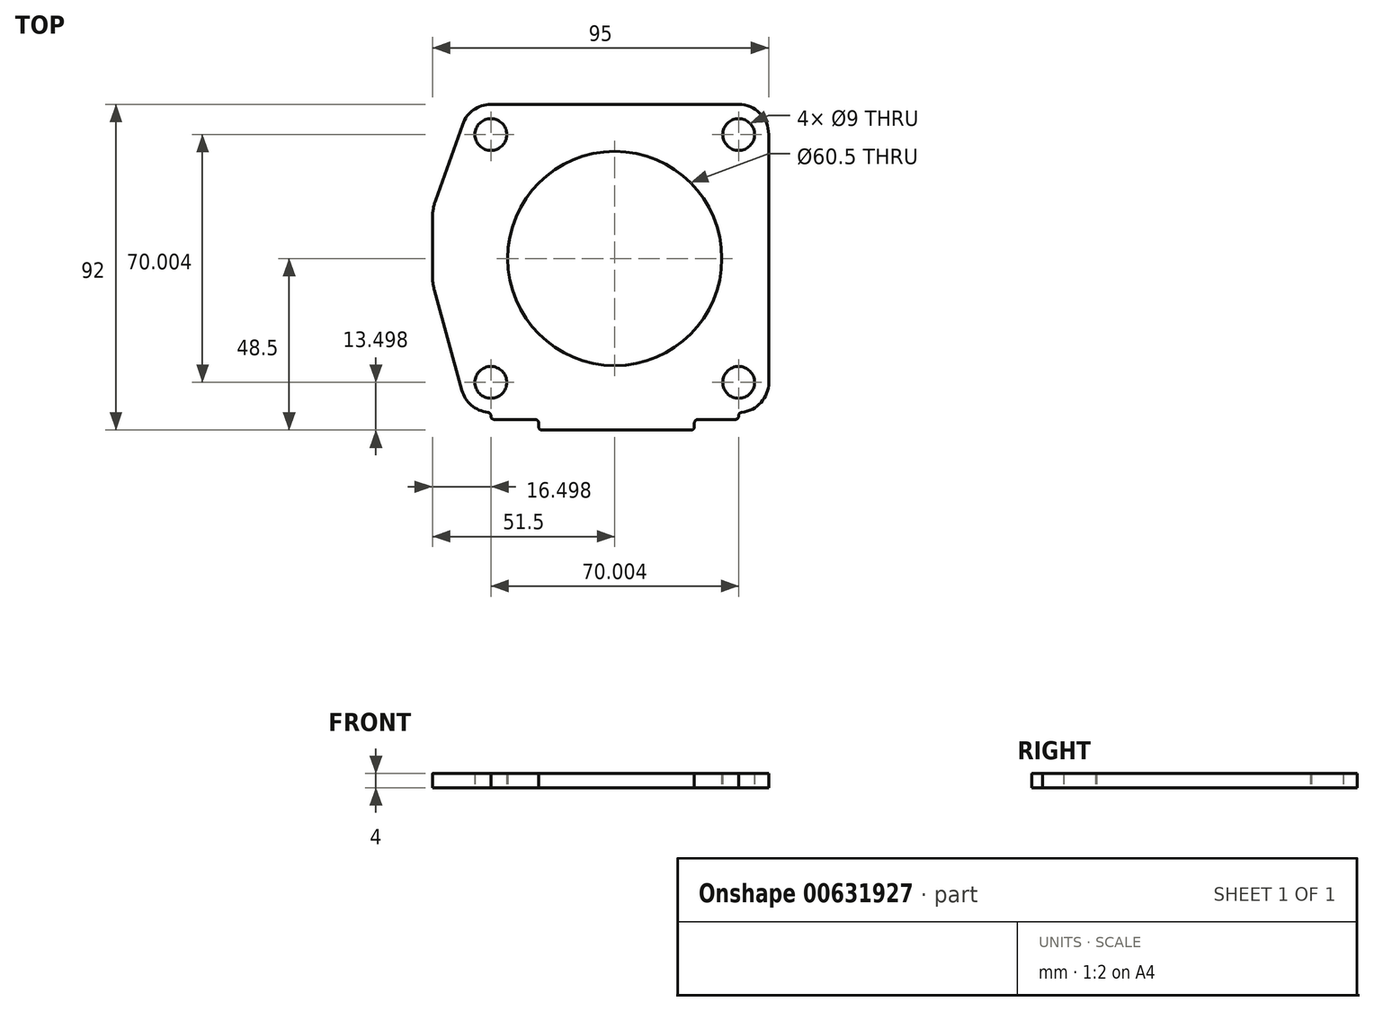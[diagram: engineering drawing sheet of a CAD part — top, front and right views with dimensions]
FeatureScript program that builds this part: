
annotation { "Feature Type Name" : "Feature", "Feature Type Description" : "" }
export const myFeature = defineFeature(function(context is Context, id is Id, definition is map)
    precondition{}
    {
        {
            var Q0;
            Q0=qCreatedBy(makeId("Top.planeOp"),FACE);
            var sketch = newSketch(context, id + "F0", { "sketchPlane" : qUnion([Q0])});
            skCircle(sketch, "E0", {"center": v(0, 0) * mm, "radius": 49.5 * mm, "construction": true});
            skCircle(sketch, "E1", {"center": v(-35, 35) * mm, "radius": 4.5 * mm});
            skLineSegment(sketch, "E2", {"start": v(-35, 35) * mm, "end": v(0, 0) * mm, "construction": true});
            skLineSegment(sketch, "E3", {"start": v(0, 49.5) * mm, "end": v(0, 0) * mm, "construction": true});
            skCircle(sketch, "E4.1.0", {"center": v(-35, -35) * mm, "radius": 4.5 * mm});
            skCircle(sketch, "E4.2.0", {"center": v(35, -35) * mm, "radius": 4.5 * mm});
            skCircle(sketch, "E4.3.0", {"center": v(35, 35) * mm, "radius": 4.5 * mm});
            skCircle(sketch, "E5", {"center": v(-35, 35) * mm, "radius": 8.5 * mm});
            skCircle(sketch, "E6", {"center": v(35, 35) * mm, "radius": 8.5 * mm});
            skCircle(sketch, "E7", {"center": v(35, -35) * mm, "radius": 8.5 * mm});
            skCircle(sketch, "E8", {"center": v(-35, -35) * mm, "radius": 8.5 * mm});
            skLineSegment(sketch, "E9", {"start": v(-35, 43.5) * mm, "end": v(35, 43.5) * mm});
            skLineSegment(sketch, "E10", {"start": v(43.5, 35) * mm, "end": v(43.5, -35) * mm});
            skLineSegment(sketch, "E11", {"start": v(35, -43.5) * mm, "end": v(-35, -43.5) * mm});
            skLineSegment(sketch, "E12", {"start": v(-43.5, -35) * mm, "end": v(-43.5, 35) * mm});
            skCircle(sketch, "E13", {"center": v(0, 0) * mm, "radius": 30.25 * mm});
            skLineSegment(sketch, "E14.bottom", {"start": v(-35, -43.5) * mm, "end": v(35, -43.5) * mm});
            skLineSegment(sketch, "E14.top", {"start": v(-35, -45.5) * mm, "end": v(35, -45.5) * mm});
            skLineSegment(sketch, "E14.left", {"start": v(-35, -43.5) * mm, "end": v(-35, -45.5) * mm});
            skLineSegment(sketch, "E14.right", {"start": v(35, -43.5) * mm, "end": v(35, -45.5) * mm});
            skLineSegment(sketch, "E15.bottom", {"start": v(-21.5, -45.5) * mm, "end": v(22.5, -45.5) * mm});
            skLineSegment(sketch, "E15.top", {"start": v(-21.5, -48.5) * mm, "end": v(22.5, -48.5) * mm});
            skLineSegment(sketch, "E15.left", {"start": v(-21.5, -45.5) * mm, "end": v(-21.5, -48.5) * mm});
            skLineSegment(sketch, "E15.right", {"start": v(22.5, -45.5) * mm, "end": v(22.5, -48.5) * mm});
            skLineSegment(sketch, "E16", {"start": v(-51.5, 14) * mm, "end": v(-51.5, -7) * mm});
            skLineSegment(sketch, "E17", {"start": v(-51.5, 14) * mm, "end": v(-43, 37.85) * mm});
            skLineSegment(sketch, "E18", {"start": v(-51.5, -7) * mm, "end": v(-43.2, -37.25) * mm});
            skSolve(sketch);
        }
        {
            var Q0;
            Q0 = qSketchRegion(id + "F0", true);
            extrude(context, id + "F1", {"entities" : qUnion([Q0]), "depth" : 4 * mm, "offsetDistance" : 25 * mm});
        }
        {
            var Q0;
            Q0=makeQuery(id+"F1.opExtrude","SWEPT_EDGE",EDGE,{"disambiguationData":[OSD([sQuery(id+"F0.wireOp",EDGE,"E16"),sQuery(id+"F0.wireOp",EDGE,"E17")])]});
            var Q1;
            Q1=makeQuery(id+"F1.opExtrude","SWEPT_EDGE",EDGE,{"disambiguationData":[OSD([sQuery(id+"F0.wireOp",EDGE,"E16"),sQuery(id+"F0.wireOp",EDGE,"E18")])]});
            fillet(context, id + "F2", {"entities" : qUnion([Q0, Q1]), "radius" : 15 * mm, "tangentPropagation" : true, "allowEdgeOverflow" : false});
        }
        {
            var Q0;
            Q0=makeQuery(id+"F1.opExtrude","SWEPT_EDGE",EDGE,{"disambiguationData":[OSD([sQuery(id+"F0.wireOp",EDGE,"E8"),sQuery(id+"F0.wireOp",EDGE,"E14.bottom"),sQuery(id+"F0.wireOp",EDGE,"E14.left")])]});
            var Q1;
            Q1=makeQuery(id+"F1.opExtrude","SWEPT_EDGE",EDGE,{"disambiguationData":[OSD([sQuery(id+"F0.wireOp",EDGE,"E14.top"),sQuery(id+"F0.wireOp",EDGE,"E15.bottom"),sQuery(id+"F0.wireOp",EDGE,"E15.left")])]});
            var Q2;
            Q2=makeQuery(id+"F1.opExtrude","SWEPT_EDGE",EDGE,{"disambiguationData":[OSD([sQuery(id+"F0.wireOp",EDGE,"E14.top"),sQuery(id+"F0.wireOp",EDGE,"E15.bottom"),sQuery(id+"F0.wireOp",EDGE,"E15.right")])]});
            var Q3;
            Q3=makeQuery(id+"F1.opExtrude","SWEPT_EDGE",EDGE,{"disambiguationData":[OSD([sQuery(id+"F0.wireOp",EDGE,"E7"),sQuery(id+"F0.wireOp",EDGE,"E14.bottom"),sQuery(id+"F0.wireOp",EDGE,"E14.right")])]});
            var Q4;
            Q4=makeQuery(id+"F1.opExtrude","SWEPT_EDGE",EDGE,{"disambiguationData":[OSD([sQuery(id+"F0.wireOp",EDGE,"E14.top"),sQuery(id+"F0.wireOp",EDGE,"E14.left")])]});
            var Q5;
            Q5=makeQuery(id+"F1.opExtrude","SWEPT_EDGE",EDGE,{"disambiguationData":[OSD([sQuery(id+"F0.wireOp",EDGE,"E15.top"),sQuery(id+"F0.wireOp",EDGE,"E15.left")])]});
            var Q6;
            Q6=makeQuery(id+"F1.opExtrude","SWEPT_EDGE",EDGE,{"disambiguationData":[OSD([sQuery(id+"F0.wireOp",EDGE,"E15.top"),sQuery(id+"F0.wireOp",EDGE,"E15.right")])]});
            var Q7;
            Q7=makeQuery(id+"F1.opExtrude","SWEPT_EDGE",EDGE,{"disambiguationData":[OSD([sQuery(id+"F0.wireOp",EDGE,"E14.top"),sQuery(id+"F0.wireOp",EDGE,"E14.right")])]});
            fillet(context, id + "F3", {"entities" : qUnion([Q0, Q1, Q2, Q3, Q4, Q5, Q6, Q7]), "radius" : 1 * mm, "tangentPropagation" : true, "defaultsChanged" : true, "vertexSettings" : [], "allowEdgeOverflow" : false});
        }
    });
